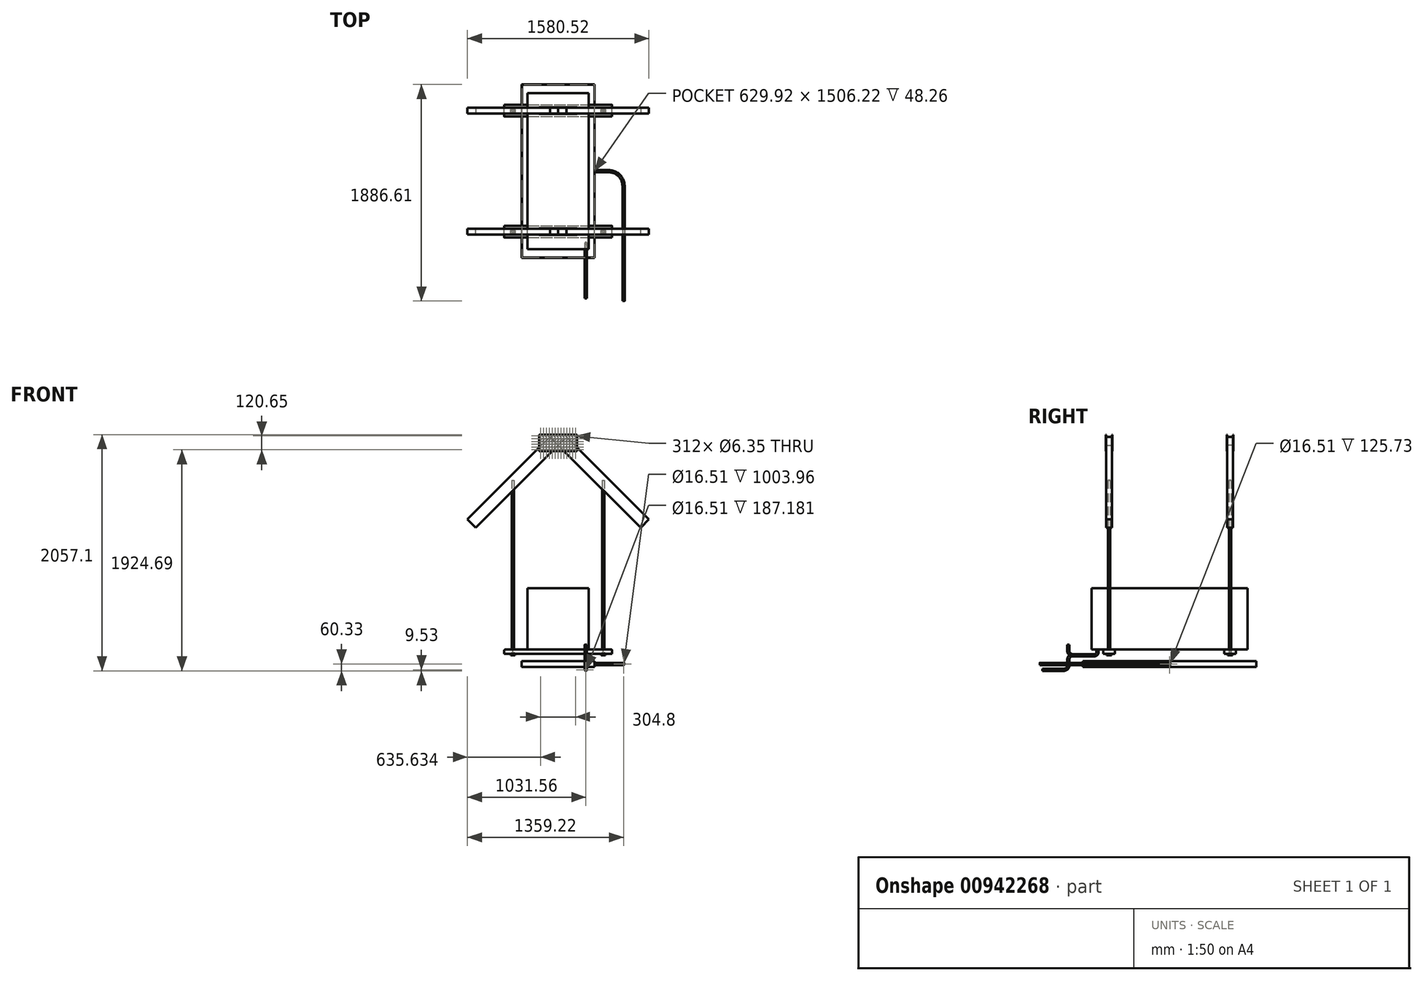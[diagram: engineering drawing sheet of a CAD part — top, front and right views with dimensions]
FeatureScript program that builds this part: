
annotation { "Feature Type Name" : "Feature", "Feature Type Description" : "" }
export const myFeature = defineFeature(function(context is Context, id is Id, definition is map)
    precondition{}
    {
        {
            var Q0;
            Q0=qCreatedBy(makeId("Front.planeOp"),FACE);
            var sketch = newSketch(context, id + "F0", { "sketchPlane" : qUnion([Q0])});
            skLineSegment(sketch, "E0.bottom", {"start": v(-266.7, 266.7) * mm, "end": v(266.7, 266.7) * mm});
            skLineSegment(sketch, "E0.top", {"start": v(-266.7, -266.7) * mm, "end": v(266.7, -266.7) * mm});
            skLineSegment(sketch, "E0.left", {"start": v(-266.7, 266.7) * mm, "end": v(-266.7, -266.7) * mm});
            skLineSegment(sketch, "E0.right", {"start": v(266.7, 266.7) * mm, "end": v(266.7, -266.7) * mm});
            skSolve(sketch);
        }
        {
            var Q0;
            Q0 = qSketchRegion(id + "F0", true);
            extrude(context, id + "F1", {"entities" : qUnion([Q0]), "endBound" : BoundingType.SYMMETRIC, "depth" : 1358.9 * mm, "offsetDistance" : 25.4 * mm});
        }
        {
            var Q0;
            Q0=makeQuery(id+"F1.opExtrude","SWEPT_FACE",FACE,{"disambiguationData":[OSD([sQuery(id+"F0.wireOp",EDGE,"E0.top")])]});
            var sketch = newSketch(context, id + "F2", { "sketchPlane" : qUnion([Q0])});
            skLineSegment(sketch, "E1.bottom", {"start": v(-469.9, 577.85) * mm, "end": v(469.9, 577.85) * mm});
            skLineSegment(sketch, "E1.top", {"start": v(-469.9, 476.25) * mm, "end": v(469.9, 476.25) * mm});
            skLineSegment(sketch, "E1.left", {"start": v(-469.9, 577.85) * mm, "end": v(-469.9, 476.25) * mm});
            skLineSegment(sketch, "E1.right", {"start": v(469.9, 577.85) * mm, "end": v(469.9, 476.25) * mm});
            skLineSegment(sketch, "E2.bottom", {"start": v(-469.9, -476.25) * mm, "end": v(469.9, -476.25) * mm});
            skLineSegment(sketch, "E2.top", {"start": v(-469.9, -577.85) * mm, "end": v(469.9, -577.85) * mm});
            skLineSegment(sketch, "E2.left", {"start": v(-469.9, -476.25) * mm, "end": v(-469.9, -577.85) * mm});
            skLineSegment(sketch, "E2.right", {"start": v(469.9, -476.25) * mm, "end": v(469.9, -577.85) * mm});
            skSolve(sketch);
        }
        {
            var Q0;
            Q0 = qSketchRegion(id + "F2", true);
            extrude(context, id + "F3", {"entities" : qUnion([Q0]), "operationType" : NewBodyOperationType.ADD, "depth" : 38.1 * mm, "offsetDistance" : 25.4 * mm});
        }
        {
            var Q0;
            {var subQ0=sQuery(id+"F2.wireOp",EDGE,"E1.top");var subQ1=sQuery(id+"F2.wireOp",EDGE,"E1.bottom");var subQ2=sQuery(id+"F2.wireOp",EDGE,"E1.right");Q0=makeQuery(id+"F3.boolean.opBoolean","SPLIT",FACE,{"disambiguationData":[TD([makeQuery(id+"F1.opExtrude","SWEPT_FACE",FACE,{"disambiguationData":[OSD([sQuery(id+"F0.wireOp",EDGE,"E0.right")])]})])],"derivedFrom":makeQuery(id+"F3.opExtrude","CAP_FACE",FACE,{"disambiguationData":[OSD([subQ1,subQ0,sQuery(id+"F2.wireOp",EDGE,"E1.left"),subQ2])],"isStart":true})});}
            var sketch = newSketch(context, id + "F4", { "sketchPlane" : qUnion([Q0])});
            skPoint(sketch, "E3", {"position": v(393.7, -527.05) * mm});
            skPoint(sketch, "E4", {"position": v(-393.7, -527.05) * mm});
            skSolve(sketch);
        }
        {
            var Q0;
            {var subQ0=sQuery(id+"F2.wireOp",EDGE,"E2.top");var subQ1=sQuery(id+"F2.wireOp",EDGE,"E2.bottom");var subQ2=sQuery(id+"F2.wireOp",EDGE,"E2.right");Q0=makeQuery(id+"F3.boolean.opBoolean","SPLIT",FACE,{"disambiguationData":[TD([makeQuery(id+"F1.opExtrude","SWEPT_FACE",FACE,{"disambiguationData":[OSD([sQuery(id+"F0.wireOp",EDGE,"E0.right")])]})])],"derivedFrom":makeQuery(id+"F3.opExtrude","CAP_FACE",FACE,{"disambiguationData":[OSD([subQ1,subQ0,sQuery(id+"F2.wireOp",EDGE,"E2.left"),subQ2])],"isStart":true})});}
            var sketch = newSketch(context, id + "F5", { "sketchPlane" : qUnion([Q0])});
            skPoint(sketch, "E5", {"position": v(393.7, 527.05) * mm});
            skPoint(sketch, "E6", {"position": v(-393.7, 527.05) * mm});
            skSolve(sketch);
        }
        {
            var Q0;
            Q0=sQuery(id+"F4.wireOp",VERTEX,"E3");
            var Q1;
            Q1=sQuery(id+"F4.wireOp",VERTEX,"E4");
            var Q2;
            Q2=sQuery(id+"F5.wireOp",VERTEX,"E5");
            var Q3;
            Q3=sQuery(id+"F5.wireOp",VERTEX,"E6");
            var Q4;
            Q4=makeQuery(id+"F1.opExtrude","SWEPT_BODY",BODY,{"disambiguationData":[OSD([sQuery(id+"F0.wireOp",EDGE,"E0.bottom"),sQuery(id+"F0.wireOp",EDGE,"E0.top"),sQuery(id+"F0.wireOp",EDGE,"E0.left"),sQuery(id+"F0.wireOp",EDGE,"E0.right")])]});
            hole(context, id + "F6", {"style" : HoleStyle.SIMPLE, "endStyle" : HoleEndStyle.THROUGH, "standardTappedOrClearance" : lookupTablePath({ "standard" : "ANSI", "size" : "3/4 (0.75)", "type" : "Drilled" }), "standardBlindInLast" : lookupTablePath({ "standard" : "ANSI", "size" : "3/4 (0.75)", "type" : "Drilled" }), "holeDiameter" : 3 / 101.6 * mm, "majorDiameter" : 6.35 * mm, "isTappedThrough" : true, "tappedDepth" : 12.7 * mm, "tapClearance" : 3, "locations" : qUnion([Q0, Q1, Q2, Q3]), "scope" : qUnion([Q4])});
        }
        {
            var Q0;
            Q0=makeQuery(id+"F3.opExtrude","CAP_EDGE",EDGE,{"disambiguationData":[OSD([sQuery(id+"F2.wireOp",EDGE,"E1.right")])],"isStart":true});
            var Q1;
            Q1=makeQuery(id+"F3.opExtrude","CAP_EDGE",EDGE,{"disambiguationData":[OSD([sQuery(id+"F2.wireOp",EDGE,"E2.right")])],"isStart":true});
            var Q2;
            Q2=makeQuery(id+"F3.opExtrude","CAP_EDGE",EDGE,{"disambiguationData":[OSD([sQuery(id+"F2.wireOp",EDGE,"E1.left")])],"isStart":true});
            var Q3;
            Q3=makeQuery(id+"F3.opExtrude","CAP_EDGE",EDGE,{"disambiguationData":[OSD([sQuery(id+"F2.wireOp",EDGE,"E2.left")])],"isStart":true});
            fillet(context, id + "F7", {"entities" : qUnion([Q0, Q1, Q2, Q3]), "radius" : 12.7 * mm, "tangentPropagation" : true, "allowEdgeOverflow" : false});
        }
        {
            var Q0;
            Q0=makeQuery(id+"F3.opExtrude","CAP_FACE",FACE,{"disambiguationData":[OSD([sQuery(id+"F2.wireOp",EDGE,"E1.bottom"),sQuery(id+"F2.wireOp",EDGE,"E1.top"),sQuery(id+"F2.wireOp",EDGE,"E1.left"),sQuery(id+"F2.wireOp",EDGE,"E1.right")])],"isStart":false});
            cPlane(context, id + "F8", {"entities" : qUnion([Q0]), "cplaneType" : CPlaneType.OFFSET, "offset" : 12.7 * mm, "width" : 152.4 * mm, "height" : 152.4 * mm});
        }
        {
            var Q0;
            Q0=qCreatedBy(id+"F8.planeOp",FACE);
            var sketch = newSketch(context, id + "F9", { "sketchPlane" : qUnion([Q0])});
            skCircle(sketch, "E7.0", {"center": v(393.7, 527.05) * mm, "radius": 9.53 * mm});
            skCircle(sketch, "E8.0", {"center": v(-393.7, 527.05) * mm, "radius": 9.53 * mm});
            skSolve(sketch);
        }
        {
            var Q0;
            Q0 = qSketchRegion(id + "F9", true);
            extrude(context, id + "F10", {"entities" : qUnion([Q0]), "operationType" : NewBodyOperationType.ADD, "oppositeDirection" : true, "depth" : 1524 * mm, "offsetDistance" : 25.4 * mm});
        }
        {
            var Q0;
            Q0=makeQuery(id+"F3.opExtrude","CAP_FACE",FACE,{"disambiguationData":[OSD([sQuery(id+"F2.wireOp",EDGE,"E2.bottom"),sQuery(id+"F2.wireOp",EDGE,"E2.top"),sQuery(id+"F2.wireOp",EDGE,"E2.left"),sQuery(id+"F2.wireOp",EDGE,"E2.right")])],"isStart":false});
            cPlane(context, id + "F11", {"entities" : qUnion([Q0]), "cplaneType" : CPlaneType.OFFSET, "offset" : 12.7 * mm, "width" : 152.4 * mm, "height" : 152.4 * mm});
        }
        {
            var Q0;
            Q0=qCreatedBy(id+"F11.planeOp",FACE);
            var sketch = newSketch(context, id + "F12", { "sketchPlane" : qUnion([Q0])});
            skCircle(sketch, "E9.0", {"center": v(-393.7, -527.05) * mm, "radius": 9.53 * mm});
            skCircle(sketch, "E10.0", {"center": v(393.7, -527.05) * mm, "radius": 9.53 * mm});
            skSolve(sketch);
        }
        {
            var Q0;
            Q0 = qSketchRegion(id + "F12", true);
            extrude(context, id + "F13", {"entities" : qUnion([Q0]), "oppositeDirection" : true, "depth" : 1524 * mm, "offsetDistance" : 25.4 * mm});
        }
        {
            var Q0;
            Q0=makeQuery(id+"F1.opExtrude","CAP_FACE",FACE,{"disambiguationData":[OSD([sQuery(id+"F0.wireOp",EDGE,"E0.bottom"),sQuery(id+"F0.wireOp",EDGE,"E0.top"),sQuery(id+"F0.wireOp",EDGE,"E0.left"),sQuery(id+"F0.wireOp",EDGE,"E0.right")])],"isStart":false});
            cPlane(context, id + "F14", {"entities" : qUnion([Q0]), "cplaneType" : CPlaneType.OFFSET, "offset" : 152.4 * mm, "oppositeDirection" : true, "width" : 152.4 * mm, "height" : 152.4 * mm});
        }
        {
            var Q0;
            Q0=qCreatedBy(id+"F14.planeOp",FACE);
            var sketch = newSketch(context, id + "F15", { "sketchPlane" : qUnion([Q0])});
            skLineSegment(sketch, "E11", {"start": v(0, 2010.8) * mm, "end": v(0, -441.63) * mm, "construction": true});
            skLineSegment(sketch, "E12", {"start": v(0, 1511.3) * mm, "end": v(718.42, 792.88) * mm});
            skLineSegment(sketch, "E13", {"start": v(718.42, 792.88) * mm, "end": v(790.26, 864.72) * mm});
            skLineSegment(sketch, "E14", {"start": v(0, 1511.3) * mm, "end": v(71.84, 1583.14) * mm});
            skLineSegment(sketch, "E15", {"start": v(790.26, 864.72) * mm, "end": v(71.84, 1583.14) * mm});
            skLineSegment(sketch, "E16", {"start": v(0, 1511.3) * mm, "end": v(-718.42, 792.88) * mm});
            skLineSegment(sketch, "E17", {"start": v(-718.42, 792.88) * mm, "end": v(-790.26, 864.72) * mm});
            skLineSegment(sketch, "E18", {"start": v(0, 1511.3) * mm, "end": v(-71.84, 1583.14) * mm});
            skLineSegment(sketch, "E19", {"start": v(-790.26, 864.72) * mm, "end": v(-71.84, 1583.14) * mm});
            skSolve(sketch);
        }
        {
            var Q0;
            Q0 = qSketchRegion(id + "F15", true);
            extrude(context, id + "F16", {"entities" : qUnion([Q0]), "endBound" : BoundingType.SYMMETRIC, "depth" : 50.8 * mm, "offsetDistance" : 25.4 * mm});
        }
        {
            var Q0;
            Q0=makeQuery(id+"F1.opExtrude","CAP_FACE",FACE,{"disambiguationData":[OSD([sQuery(id+"F0.wireOp",EDGE,"E0.bottom"),sQuery(id+"F0.wireOp",EDGE,"E0.top"),sQuery(id+"F0.wireOp",EDGE,"E0.left"),sQuery(id+"F0.wireOp",EDGE,"E0.right")])],"isStart":false});
            cPlane(context, id + "F17", {"entities" : qUnion([Q0]), "cplaneType" : CPlaneType.OFFSET, "offset" : 679.45 * mm, "oppositeDirection" : true, "width" : 152.4 * mm, "height" : 152.4 * mm});
        }
        {
            var Q0;
            Q0=makeQuery(id+"F16.opExtrude","SWEPT_BODY",BODY,{"disambiguationData":[OSD([sQuery(id+"F15.wireOp",EDGE,"E12"),sQuery(id+"F15.wireOp",EDGE,"E13"),sQuery(id+"F15.wireOp",EDGE,"E14"),sQuery(id+"F15.wireOp",EDGE,"E15")])]});
            var Q1;
            Q1=makeQuery(id+"F16.opExtrude","SWEPT_BODY",BODY,{"disambiguationData":[OSD([sQuery(id+"F15.wireOp",EDGE,"E16"),sQuery(id+"F15.wireOp",EDGE,"E17"),sQuery(id+"F15.wireOp",EDGE,"E18"),sQuery(id+"F15.wireOp",EDGE,"E19")])]});
            var Q2;
            Q2=qCreatedBy(id+"F17.planeOp",FACE);
            mirror(context, id + "F18", {"entities" : qUnion([Q0, Q1]), "mirrorPlane" : qUnion([Q2])});
        }
        {
            var Q0;
            Q0=makeQuery(id+"F16.opExtrude","CAP_FACE",FACE,{"disambiguationData":[OSD([sQuery(id+"F15.wireOp",EDGE,"E12"),sQuery(id+"F15.wireOp",EDGE,"E13"),sQuery(id+"F15.wireOp",EDGE,"E14"),sQuery(id+"F15.wireOp",EDGE,"E15")])],"isStart":false});
            var sketch = newSketch(context, id + "F19", { "sketchPlane" : qUnion([Q0])});
            skLineSegment(sketch, "E20.bottom", {"start": v(-165.1, 1603.07) * mm, "end": v(165.1, 1603.07) * mm});
            skLineSegment(sketch, "E20.top", {"start": v(-165.1, 1460.5) * mm, "end": v(165.1, 1460.5) * mm});
            skLineSegment(sketch, "E20.left", {"start": v(-165.1, 1603.07) * mm, "end": v(-165.1, 1460.5) * mm});
            skLineSegment(sketch, "E20.right", {"start": v(165.1, 1603.07) * mm, "end": v(165.1, 1460.5) * mm});
            skCircle(sketch, "E21", {"center": v(-154.63, 1470.66) * mm, "radius": 3.18 * mm});
            skCircle(sketch, "E22.0.1.0", {"center": v(-154.63, 1494.8) * mm, "radius": 3.18 * mm});
            skCircle(sketch, "E22.0.2.0", {"center": v(-154.63, 1518.92) * mm, "radius": 3.18 * mm});
            skCircle(sketch, "E22.0.3.0", {"center": v(-154.63, 1543.05) * mm, "radius": 3.18 * mm});
            skCircle(sketch, "E22.0.4.0", {"center": v(-154.63, 1567.18) * mm, "radius": 3.18 * mm});
            skCircle(sketch, "E22.0.5.0", {"center": v(-154.63, 1591.3) * mm, "radius": 3.18 * mm});
            skCircle(sketch, "E22.1.0.0", {"center": v(-129.23, 1470.66) * mm, "radius": 3.18 * mm});
            skCircle(sketch, "E22.1.1.0", {"center": v(-129.23, 1494.8) * mm, "radius": 3.18 * mm});
            skCircle(sketch, "E22.1.2.0", {"center": v(-129.23, 1518.92) * mm, "radius": 3.18 * mm});
            skCircle(sketch, "E22.1.3.0", {"center": v(-129.23, 1543.05) * mm, "radius": 3.18 * mm});
            skCircle(sketch, "E22.1.4.0", {"center": v(-129.23, 1567.18) * mm, "radius": 3.18 * mm});
            skCircle(sketch, "E22.1.5.0", {"center": v(-129.23, 1591.3) * mm, "radius": 3.18 * mm});
            skCircle(sketch, "E22.2.0.0", {"center": v(-103.83, 1470.66) * mm, "radius": 3.18 * mm});
            skCircle(sketch, "E22.2.1.0", {"center": v(-103.83, 1494.8) * mm, "radius": 3.18 * mm});
            skCircle(sketch, "E22.2.2.0", {"center": v(-103.83, 1518.92) * mm, "radius": 3.18 * mm});
            skCircle(sketch, "E22.2.3.0", {"center": v(-103.83, 1543.05) * mm, "radius": 3.18 * mm});
            skCircle(sketch, "E22.2.4.0", {"center": v(-103.83, 1567.18) * mm, "radius": 3.18 * mm});
            skCircle(sketch, "E22.2.5.0", {"center": v(-103.83, 1591.3) * mm, "radius": 3.18 * mm});
            skCircle(sketch, "E22.3.0.0", {"center": v(-78.43, 1470.66) * mm, "radius": 3.18 * mm});
            skCircle(sketch, "E22.3.1.0", {"center": v(-78.43, 1494.8) * mm, "radius": 3.18 * mm});
            skCircle(sketch, "E22.3.2.0", {"center": v(-78.43, 1518.92) * mm, "radius": 3.18 * mm});
            skCircle(sketch, "E22.3.3.0", {"center": v(-78.43, 1543.05) * mm, "radius": 3.18 * mm});
            skCircle(sketch, "E22.3.4.0", {"center": v(-78.43, 1567.18) * mm, "radius": 3.18 * mm});
            skCircle(sketch, "E22.3.5.0", {"center": v(-78.43, 1591.3) * mm, "radius": 3.18 * mm});
            skCircle(sketch, "E22.4.0.0", {"center": v(-53.03, 1470.66) * mm, "radius": 3.18 * mm});
            skCircle(sketch, "E22.4.1.0", {"center": v(-53.03, 1494.8) * mm, "radius": 3.18 * mm});
            skCircle(sketch, "E22.4.2.0", {"center": v(-53.03, 1518.92) * mm, "radius": 3.18 * mm});
            skCircle(sketch, "E22.4.3.0", {"center": v(-53.03, 1543.05) * mm, "radius": 3.18 * mm});
            skCircle(sketch, "E22.4.4.0", {"center": v(-53.03, 1567.18) * mm, "radius": 3.18 * mm});
            skCircle(sketch, "E22.4.5.0", {"center": v(-53.03, 1591.3) * mm, "radius": 3.18 * mm});
            skCircle(sketch, "E22.5.0.0", {"center": v(-27.63, 1470.66) * mm, "radius": 3.18 * mm});
            skCircle(sketch, "E22.5.1.0", {"center": v(-27.63, 1494.8) * mm, "radius": 3.18 * mm});
            skCircle(sketch, "E22.5.2.0", {"center": v(-27.63, 1518.92) * mm, "radius": 3.18 * mm});
            skCircle(sketch, "E22.5.3.0", {"center": v(-27.63, 1543.05) * mm, "radius": 3.18 * mm});
            skCircle(sketch, "E22.5.4.0", {"center": v(-27.63, 1567.18) * mm, "radius": 3.18 * mm});
            skCircle(sketch, "E22.5.5.0", {"center": v(-27.63, 1591.3) * mm, "radius": 3.18 * mm});
            skCircle(sketch, "E22.6.0.0", {"center": v(-2.23, 1470.66) * mm, "radius": 3.18 * mm});
            skCircle(sketch, "E22.6.1.0", {"center": v(-2.23, 1494.8) * mm, "radius": 3.18 * mm});
            skCircle(sketch, "E22.6.2.0", {"center": v(-2.23, 1518.92) * mm, "radius": 3.18 * mm});
            skCircle(sketch, "E22.6.3.0", {"center": v(-2.23, 1543.05) * mm, "radius": 3.18 * mm});
            skCircle(sketch, "E22.6.4.0", {"center": v(-2.23, 1567.18) * mm, "radius": 3.18 * mm});
            skCircle(sketch, "E22.6.5.0", {"center": v(-2.23, 1591.3) * mm, "radius": 3.18 * mm});
            skCircle(sketch, "E22.7.0.0", {"center": v(23.17, 1470.66) * mm, "radius": 3.18 * mm});
            skCircle(sketch, "E22.7.1.0", {"center": v(23.17, 1494.8) * mm, "radius": 3.18 * mm});
            skCircle(sketch, "E22.7.2.0", {"center": v(23.17, 1518.92) * mm, "radius": 3.18 * mm});
            skCircle(sketch, "E22.7.3.0", {"center": v(23.17, 1543.05) * mm, "radius": 3.18 * mm});
            skCircle(sketch, "E22.7.4.0", {"center": v(23.17, 1567.18) * mm, "radius": 3.18 * mm});
            skCircle(sketch, "E22.7.5.0", {"center": v(23.17, 1591.3) * mm, "radius": 3.18 * mm});
            skCircle(sketch, "E22.8.0.0", {"center": v(48.57, 1470.66) * mm, "radius": 3.18 * mm});
            skCircle(sketch, "E22.8.1.0", {"center": v(48.57, 1494.8) * mm, "radius": 3.18 * mm});
            skCircle(sketch, "E22.8.2.0", {"center": v(48.57, 1518.92) * mm, "radius": 3.18 * mm});
            skCircle(sketch, "E22.8.3.0", {"center": v(48.57, 1543.05) * mm, "radius": 3.18 * mm});
            skCircle(sketch, "E22.8.4.0", {"center": v(48.57, 1567.18) * mm, "radius": 3.18 * mm});
            skCircle(sketch, "E22.8.5.0", {"center": v(48.57, 1591.3) * mm, "radius": 3.18 * mm});
            skCircle(sketch, "E22.9.0.0", {"center": v(73.97, 1470.66) * mm, "radius": 3.18 * mm});
            skCircle(sketch, "E22.9.1.0", {"center": v(73.97, 1494.8) * mm, "radius": 3.18 * mm});
            skCircle(sketch, "E22.9.2.0", {"center": v(73.97, 1518.92) * mm, "radius": 3.18 * mm});
            skCircle(sketch, "E22.9.3.0", {"center": v(73.97, 1543.05) * mm, "radius": 3.18 * mm});
            skCircle(sketch, "E22.9.4.0", {"center": v(73.97, 1567.18) * mm, "radius": 3.18 * mm});
            skCircle(sketch, "E22.9.5.0", {"center": v(73.97, 1591.3) * mm, "radius": 3.18 * mm});
            skCircle(sketch, "E22.10.0.0", {"center": v(99.37, 1470.66) * mm, "radius": 3.18 * mm});
            skCircle(sketch, "E22.10.1.0", {"center": v(99.37, 1494.8) * mm, "radius": 3.18 * mm});
            skCircle(sketch, "E22.10.2.0", {"center": v(99.37, 1518.92) * mm, "radius": 3.18 * mm});
            skCircle(sketch, "E22.10.3.0", {"center": v(99.37, 1543.05) * mm, "radius": 3.18 * mm});
            skCircle(sketch, "E22.10.4.0", {"center": v(99.37, 1567.18) * mm, "radius": 3.18 * mm});
            skCircle(sketch, "E22.10.5.0", {"center": v(99.37, 1591.3) * mm, "radius": 3.18 * mm});
            skCircle(sketch, "E22.11.0.0", {"center": v(124.77, 1470.66) * mm, "radius": 3.18 * mm});
            skCircle(sketch, "E22.11.1.0", {"center": v(124.77, 1494.8) * mm, "radius": 3.18 * mm});
            skCircle(sketch, "E22.11.2.0", {"center": v(124.77, 1518.92) * mm, "radius": 3.18 * mm});
            skCircle(sketch, "E22.11.3.0", {"center": v(124.77, 1543.05) * mm, "radius": 3.18 * mm});
            skCircle(sketch, "E22.11.4.0", {"center": v(124.77, 1567.18) * mm, "radius": 3.18 * mm});
            skCircle(sketch, "E22.11.5.0", {"center": v(124.77, 1591.3) * mm, "radius": 3.18 * mm});
            skCircle(sketch, "E22.12.0.0", {"center": v(150.17, 1470.66) * mm, "radius": 3.18 * mm});
            skCircle(sketch, "E22.12.1.0", {"center": v(150.17, 1494.8) * mm, "radius": 3.18 * mm});
            skCircle(sketch, "E22.12.2.0", {"center": v(150.17, 1518.92) * mm, "radius": 3.18 * mm});
            skCircle(sketch, "E22.12.3.0", {"center": v(150.17, 1543.05) * mm, "radius": 3.18 * mm});
            skCircle(sketch, "E22.12.4.0", {"center": v(150.17, 1567.18) * mm, "radius": 3.18 * mm});
            skCircle(sketch, "E22.12.5.0", {"center": v(150.17, 1591.3) * mm, "radius": 3.18 * mm});
            skLineSegment(sketch, "E22.direction1", {"start": v(-154.63, 1470.66) * mm, "end": v(-129.23, 1470.66) * mm, "construction": true});
            skLineSegment(sketch, "E22.direction2", {"start": v(-154.63, 1470.66) * mm, "end": v(-154.63, 1494.8) * mm, "construction": true});
            skSolve(sketch);
        }
        {
            var Q0;
            Q0 = qSketchRegion(id + "F19", true);
            extrude(context, id + "F20", {"entities" : qUnion([Q0]), "depth" : 2.54 * mm, "offsetDistance" : 25.4 * mm});
        }
        {
            var Q0;
            Q0=makeQuery(id+"F16.opExtrude","CAP_FACE",FACE,{"disambiguationData":[OSD([sQuery(id+"F15.wireOp",EDGE,"E12"),sQuery(id+"F15.wireOp",EDGE,"E13"),sQuery(id+"F15.wireOp",EDGE,"E14"),sQuery(id+"F15.wireOp",EDGE,"E15")])],"isStart":true});
            var sketch = newSketch(context, id + "F21", { "sketchPlane" : qUnion([Q0])});
            skLineSegment(sketch, "E23.0.0", {"start": v(165.1, 1460.5) * mm, "end": v(165.1, 1603.07) * mm});
            skLineSegment(sketch, "E23.0.1", {"start": v(165.1, 1603.07) * mm, "end": v(-165.1, 1603.07) * mm});
            skLineSegment(sketch, "E23.0.2", {"start": v(-165.1, 1603.07) * mm, "end": v(-165.1, 1460.5) * mm});
            skLineSegment(sketch, "E23.0.3", {"start": v(-165.1, 1460.5) * mm, "end": v(165.1, 1460.5) * mm});
            skCircle(sketch, "E24.0", {"center": v(154.63, 1591.3) * mm, "radius": 3.18 * mm});
            skCircle(sketch, "E25.0.1.0", {"center": v(154.63, 1567.18) * mm, "radius": 3.18 * mm});
            skCircle(sketch, "E25.0.2.0", {"center": v(154.63, 1543.05) * mm, "radius": 3.18 * mm});
            skCircle(sketch, "E25.0.3.0", {"center": v(154.63, 1518.92) * mm, "radius": 3.18 * mm});
            skCircle(sketch, "E25.0.4.0", {"center": v(154.63, 1494.8) * mm, "radius": 3.18 * mm});
            skCircle(sketch, "E25.0.5.0", {"center": v(154.63, 1470.66) * mm, "radius": 3.18 * mm});
            skCircle(sketch, "E25.1.0.0", {"center": v(129.23, 1591.3) * mm, "radius": 3.18 * mm});
            skCircle(sketch, "E25.1.1.0", {"center": v(129.23, 1567.18) * mm, "radius": 3.18 * mm});
            skCircle(sketch, "E25.1.2.0", {"center": v(129.23, 1543.05) * mm, "radius": 3.18 * mm});
            skCircle(sketch, "E25.1.3.0", {"center": v(129.23, 1518.92) * mm, "radius": 3.18 * mm});
            skCircle(sketch, "E25.1.4.0", {"center": v(129.23, 1494.8) * mm, "radius": 3.18 * mm});
            skCircle(sketch, "E25.1.5.0", {"center": v(129.23, 1470.66) * mm, "radius": 3.18 * mm});
            skCircle(sketch, "E25.2.0.0", {"center": v(103.83, 1591.3) * mm, "radius": 3.18 * mm});
            skCircle(sketch, "E25.2.1.0", {"center": v(103.83, 1567.18) * mm, "radius": 3.18 * mm});
            skCircle(sketch, "E25.2.2.0", {"center": v(103.83, 1543.05) * mm, "radius": 3.18 * mm});
            skCircle(sketch, "E25.2.3.0", {"center": v(103.83, 1518.92) * mm, "radius": 3.18 * mm});
            skCircle(sketch, "E25.2.4.0", {"center": v(103.83, 1494.8) * mm, "radius": 3.18 * mm});
            skCircle(sketch, "E25.2.5.0", {"center": v(103.83, 1470.66) * mm, "radius": 3.18 * mm});
            skCircle(sketch, "E25.3.0.0", {"center": v(78.43, 1591.3) * mm, "radius": 3.18 * mm});
            skCircle(sketch, "E25.3.1.0", {"center": v(78.43, 1567.18) * mm, "radius": 3.18 * mm});
            skCircle(sketch, "E25.3.2.0", {"center": v(78.43, 1543.05) * mm, "radius": 3.18 * mm});
            skCircle(sketch, "E25.3.3.0", {"center": v(78.43, 1518.92) * mm, "radius": 3.18 * mm});
            skCircle(sketch, "E25.3.4.0", {"center": v(78.43, 1494.8) * mm, "radius": 3.18 * mm});
            skCircle(sketch, "E25.3.5.0", {"center": v(78.43, 1470.66) * mm, "radius": 3.18 * mm});
            skCircle(sketch, "E25.4.0.0", {"center": v(53.03, 1591.3) * mm, "radius": 3.18 * mm});
            skCircle(sketch, "E25.4.1.0", {"center": v(53.03, 1567.18) * mm, "radius": 3.18 * mm});
            skCircle(sketch, "E25.4.2.0", {"center": v(53.03, 1543.05) * mm, "radius": 3.18 * mm});
            skCircle(sketch, "E25.4.3.0", {"center": v(53.03, 1518.92) * mm, "radius": 3.18 * mm});
            skCircle(sketch, "E25.4.4.0", {"center": v(53.03, 1494.8) * mm, "radius": 3.18 * mm});
            skCircle(sketch, "E25.4.5.0", {"center": v(53.03, 1470.66) * mm, "radius": 3.18 * mm});
            skCircle(sketch, "E25.5.0.0", {"center": v(27.63, 1591.3) * mm, "radius": 3.18 * mm});
            skCircle(sketch, "E25.5.1.0", {"center": v(27.63, 1567.18) * mm, "radius": 3.18 * mm});
            skCircle(sketch, "E25.5.2.0", {"center": v(27.63, 1543.05) * mm, "radius": 3.18 * mm});
            skCircle(sketch, "E25.5.3.0", {"center": v(27.63, 1518.92) * mm, "radius": 3.18 * mm});
            skCircle(sketch, "E25.5.4.0", {"center": v(27.63, 1494.8) * mm, "radius": 3.18 * mm});
            skCircle(sketch, "E25.5.5.0", {"center": v(27.63, 1470.66) * mm, "radius": 3.18 * mm});
            skCircle(sketch, "E25.6.0.0", {"center": v(2.23, 1591.3) * mm, "radius": 3.18 * mm});
            skCircle(sketch, "E25.6.1.0", {"center": v(2.23, 1567.18) * mm, "radius": 3.18 * mm});
            skCircle(sketch, "E25.6.2.0", {"center": v(2.23, 1543.05) * mm, "radius": 3.18 * mm});
            skCircle(sketch, "E25.6.3.0", {"center": v(2.23, 1518.92) * mm, "radius": 3.18 * mm});
            skCircle(sketch, "E25.6.4.0", {"center": v(2.23, 1494.8) * mm, "radius": 3.18 * mm});
            skCircle(sketch, "E25.6.5.0", {"center": v(2.23, 1470.66) * mm, "radius": 3.18 * mm});
            skCircle(sketch, "E25.7.0.0", {"center": v(-23.17, 1591.3) * mm, "radius": 3.18 * mm});
            skCircle(sketch, "E25.7.1.0", {"center": v(-23.17, 1567.18) * mm, "radius": 3.18 * mm});
            skCircle(sketch, "E25.7.2.0", {"center": v(-23.17, 1543.05) * mm, "radius": 3.18 * mm});
            skCircle(sketch, "E25.7.3.0", {"center": v(-23.17, 1518.92) * mm, "radius": 3.18 * mm});
            skCircle(sketch, "E25.7.4.0", {"center": v(-23.17, 1494.8) * mm, "radius": 3.18 * mm});
            skCircle(sketch, "E25.7.5.0", {"center": v(-23.17, 1470.66) * mm, "radius": 3.18 * mm});
            skCircle(sketch, "E25.8.0.0", {"center": v(-48.57, 1591.3) * mm, "radius": 3.18 * mm});
            skCircle(sketch, "E25.8.1.0", {"center": v(-48.57, 1567.18) * mm, "radius": 3.18 * mm});
            skCircle(sketch, "E25.8.2.0", {"center": v(-48.57, 1543.05) * mm, "radius": 3.18 * mm});
            skCircle(sketch, "E25.8.3.0", {"center": v(-48.57, 1518.92) * mm, "radius": 3.18 * mm});
            skCircle(sketch, "E25.8.4.0", {"center": v(-48.57, 1494.8) * mm, "radius": 3.18 * mm});
            skCircle(sketch, "E25.8.5.0", {"center": v(-48.57, 1470.66) * mm, "radius": 3.18 * mm});
            skCircle(sketch, "E25.9.0.0", {"center": v(-73.97, 1591.3) * mm, "radius": 3.18 * mm});
            skCircle(sketch, "E25.9.1.0", {"center": v(-73.97, 1567.18) * mm, "radius": 3.18 * mm});
            skCircle(sketch, "E25.9.2.0", {"center": v(-73.97, 1543.05) * mm, "radius": 3.18 * mm});
            skCircle(sketch, "E25.9.3.0", {"center": v(-73.97, 1518.92) * mm, "radius": 3.18 * mm});
            skCircle(sketch, "E25.9.4.0", {"center": v(-73.97, 1494.8) * mm, "radius": 3.18 * mm});
            skCircle(sketch, "E25.9.5.0", {"center": v(-73.97, 1470.66) * mm, "radius": 3.18 * mm});
            skCircle(sketch, "E25.10.0.0", {"center": v(-99.37, 1591.3) * mm, "radius": 3.18 * mm});
            skCircle(sketch, "E25.10.1.0", {"center": v(-99.37, 1567.18) * mm, "radius": 3.18 * mm});
            skCircle(sketch, "E25.10.2.0", {"center": v(-99.37, 1543.05) * mm, "radius": 3.18 * mm});
            skCircle(sketch, "E25.10.3.0", {"center": v(-99.37, 1518.92) * mm, "radius": 3.18 * mm});
            skCircle(sketch, "E25.10.4.0", {"center": v(-99.37, 1494.8) * mm, "radius": 3.18 * mm});
            skCircle(sketch, "E25.10.5.0", {"center": v(-99.37, 1470.66) * mm, "radius": 3.18 * mm});
            skCircle(sketch, "E25.11.0.0", {"center": v(-124.77, 1591.3) * mm, "radius": 3.18 * mm});
            skCircle(sketch, "E25.11.1.0", {"center": v(-124.77, 1567.18) * mm, "radius": 3.18 * mm});
            skCircle(sketch, "E25.11.2.0", {"center": v(-124.77, 1543.05) * mm, "radius": 3.18 * mm});
            skCircle(sketch, "E25.11.3.0", {"center": v(-124.77, 1518.92) * mm, "radius": 3.18 * mm});
            skCircle(sketch, "E25.11.4.0", {"center": v(-124.77, 1494.8) * mm, "radius": 3.18 * mm});
            skCircle(sketch, "E25.11.5.0", {"center": v(-124.77, 1470.66) * mm, "radius": 3.18 * mm});
            skCircle(sketch, "E25.12.0.0", {"center": v(-150.17, 1591.3) * mm, "radius": 3.18 * mm});
            skCircle(sketch, "E25.12.1.0", {"center": v(-150.17, 1567.18) * mm, "radius": 3.18 * mm});
            skCircle(sketch, "E25.12.2.0", {"center": v(-150.17, 1543.05) * mm, "radius": 3.18 * mm});
            skCircle(sketch, "E25.12.3.0", {"center": v(-150.17, 1518.92) * mm, "radius": 3.18 * mm});
            skCircle(sketch, "E25.12.4.0", {"center": v(-150.17, 1494.8) * mm, "radius": 3.18 * mm});
            skCircle(sketch, "E25.12.5.0", {"center": v(-150.17, 1470.66) * mm, "radius": 3.18 * mm});
            skLineSegment(sketch, "E25.direction1", {"start": v(154.63, 1591.3) * mm, "end": v(129.23, 1591.3) * mm, "construction": true});
            skLineSegment(sketch, "E25.direction2", {"start": v(154.63, 1591.3) * mm, "end": v(154.63, 1567.18) * mm, "construction": true});
            skSolve(sketch);
        }
        {
            var Q0;
            Q0 = qSketchRegion(id + "F21", true);
            extrude(context, id + "F22", {"entities" : qUnion([Q0]), "depth" : 2.54 * mm, "offsetDistance" : 25.4 * mm});
        }
        {
            var Q0;
            Q0=makeQuery(id+"F20.opExtrude","SWEPT_BODY",BODY,{"disambiguationData":[OSD([sQuery(id+"F19.wireOp",EDGE,"E20.bottom"),sQuery(id+"F19.wireOp",EDGE,"E20.top"),sQuery(id+"F19.wireOp",EDGE,"E20.left"),sQuery(id+"F19.wireOp",EDGE,"E20.right"),sQuery(id+"F19.wireOp",EDGE,"E21"),sQuery(id+"F19.wireOp",EDGE,"E22.0.1.0"),sQuery(id+"F19.wireOp",EDGE,"E22.0.2.0"),sQuery(id+"F19.wireOp",EDGE,"E22.0.3.0"),sQuery(id+"F19.wireOp",EDGE,"E22.0.4.0"),sQuery(id+"F19.wireOp",EDGE,"E22.0.5.0"),sQuery(id+"F19.wireOp",EDGE,"E22.1.0.0"),sQuery(id+"F19.wireOp",EDGE,"E22.1.1.0"),sQuery(id+"F19.wireOp",EDGE,"E22.1.2.0"),sQuery(id+"F19.wireOp",EDGE,"E22.1.3.0"),sQuery(id+"F19.wireOp",EDGE,"E22.1.4.0"),sQuery(id+"F19.wireOp",EDGE,"E22.1.5.0"),sQuery(id+"F19.wireOp",EDGE,"E22.2.0.0"),sQuery(id+"F19.wireOp",EDGE,"E22.2.1.0"),sQuery(id+"F19.wireOp",EDGE,"E22.2.2.0"),sQuery(id+"F19.wireOp",EDGE,"E22.2.3.0"),sQuery(id+"F19.wireOp",EDGE,"E22.2.4.0"),sQuery(id+"F19.wireOp",EDGE,"E22.2.5.0"),sQuery(id+"F19.wireOp",EDGE,"E22.3.0.0"),sQuery(id+"F19.wireOp",EDGE,"E22.3.1.0"),sQuery(id+"F19.wireOp",EDGE,"E22.3.2.0"),sQuery(id+"F19.wireOp",EDGE,"E22.3.3.0"),sQuery(id+"F19.wireOp",EDGE,"E22.3.4.0"),sQuery(id+"F19.wireOp",EDGE,"E22.3.5.0"),sQuery(id+"F19.wireOp",EDGE,"E22.4.0.0"),sQuery(id+"F19.wireOp",EDGE,"E22.4.1.0"),sQuery(id+"F19.wireOp",EDGE,"E22.4.2.0"),sQuery(id+"F19.wireOp",EDGE,"E22.4.3.0"),sQuery(id+"F19.wireOp",EDGE,"E22.4.4.0"),sQuery(id+"F19.wireOp",EDGE,"E22.4.5.0"),sQuery(id+"F19.wireOp",EDGE,"E22.5.0.0"),sQuery(id+"F19.wireOp",EDGE,"E22.5.1.0"),sQuery(id+"F19.wireOp",EDGE,"E22.5.2.0"),sQuery(id+"F19.wireOp",EDGE,"E22.5.3.0"),sQuery(id+"F19.wireOp",EDGE,"E22.5.4.0"),sQuery(id+"F19.wireOp",EDGE,"E22.5.5.0"),sQuery(id+"F19.wireOp",EDGE,"E22.6.0.0"),sQuery(id+"F19.wireOp",EDGE,"E22.6.1.0"),sQuery(id+"F19.wireOp",EDGE,"E22.6.2.0"),sQuery(id+"F19.wireOp",EDGE,"E22.6.3.0"),sQuery(id+"F19.wireOp",EDGE,"E22.6.4.0"),sQuery(id+"F19.wireOp",EDGE,"E22.6.5.0"),sQuery(id+"F19.wireOp",EDGE,"E22.7.0.0"),sQuery(id+"F19.wireOp",EDGE,"E22.7.1.0"),sQuery(id+"F19.wireOp",EDGE,"E22.7.2.0"),sQuery(id+"F19.wireOp",EDGE,"E22.7.3.0"),sQuery(id+"F19.wireOp",EDGE,"E22.7.4.0"),sQuery(id+"F19.wireOp",EDGE,"E22.7.5.0"),sQuery(id+"F19.wireOp",EDGE,"E22.8.0.0"),sQuery(id+"F19.wireOp",EDGE,"E22.8.1.0"),sQuery(id+"F19.wireOp",EDGE,"E22.8.2.0"),sQuery(id+"F19.wireOp",EDGE,"E22.8.3.0"),sQuery(id+"F19.wireOp",EDGE,"E22.8.4.0"),sQuery(id+"F19.wireOp",EDGE,"E22.8.5.0"),sQuery(id+"F19.wireOp",EDGE,"E22.9.0.0"),sQuery(id+"F19.wireOp",EDGE,"E22.9.1.0"),sQuery(id+"F19.wireOp",EDGE,"E22.9.2.0"),sQuery(id+"F19.wireOp",EDGE,"E22.9.3.0"),sQuery(id+"F19.wireOp",EDGE,"E22.9.4.0"),sQuery(id+"F19.wireOp",EDGE,"E22.9.5.0"),sQuery(id+"F19.wireOp",EDGE,"E22.10.0.0"),sQuery(id+"F19.wireOp",EDGE,"E22.10.1.0"),sQuery(id+"F19.wireOp",EDGE,"E22.10.2.0"),sQuery(id+"F19.wireOp",EDGE,"E22.10.3.0"),sQuery(id+"F19.wireOp",EDGE,"E22.10.4.0"),sQuery(id+"F19.wireOp",EDGE,"E22.10.5.0"),sQuery(id+"F19.wireOp",EDGE,"E22.11.0.0"),sQuery(id+"F19.wireOp",EDGE,"E22.11.1.0"),sQuery(id+"F19.wireOp",EDGE,"E22.11.2.0"),sQuery(id+"F19.wireOp",EDGE,"E22.11.3.0"),sQuery(id+"F19.wireOp",EDGE,"E22.11.4.0"),sQuery(id+"F19.wireOp",EDGE,"E22.11.5.0"),sQuery(id+"F19.wireOp",EDGE,"E22.12.0.0"),sQuery(id+"F19.wireOp",EDGE,"E22.12.1.0"),sQuery(id+"F19.wireOp",EDGE,"E22.12.2.0"),sQuery(id+"F19.wireOp",EDGE,"E22.12.3.0"),sQuery(id+"F19.wireOp",EDGE,"E22.12.4.0"),sQuery(id+"F19.wireOp",EDGE,"E22.12.5.0")])]});
            var Q1;
            Q1=makeQuery(id+"F22.opExtrude","SWEPT_BODY",BODY,{"disambiguationData":[OSD([sQuery(id+"F21.wireOp",EDGE,"E23.0.0"),sQuery(id+"F21.wireOp",EDGE,"E23.0.1"),sQuery(id+"F21.wireOp",EDGE,"E23.0.2"),sQuery(id+"F21.wireOp",EDGE,"E23.0.3"),sQuery(id+"F21.wireOp",EDGE,"E24.0"),sQuery(id+"F21.wireOp",EDGE,"E25.0.1.0"),sQuery(id+"F21.wireOp",EDGE,"E25.0.2.0"),sQuery(id+"F21.wireOp",EDGE,"E25.0.3.0"),sQuery(id+"F21.wireOp",EDGE,"E25.0.4.0"),sQuery(id+"F21.wireOp",EDGE,"E25.0.5.0"),sQuery(id+"F21.wireOp",EDGE,"E25.1.0.0"),sQuery(id+"F21.wireOp",EDGE,"E25.1.1.0"),sQuery(id+"F21.wireOp",EDGE,"E25.1.2.0"),sQuery(id+"F21.wireOp",EDGE,"E25.1.3.0"),sQuery(id+"F21.wireOp",EDGE,"E25.1.4.0"),sQuery(id+"F21.wireOp",EDGE,"E25.1.5.0"),sQuery(id+"F21.wireOp",EDGE,"E25.2.0.0"),sQuery(id+"F21.wireOp",EDGE,"E25.2.1.0"),sQuery(id+"F21.wireOp",EDGE,"E25.2.2.0"),sQuery(id+"F21.wireOp",EDGE,"E25.2.3.0"),sQuery(id+"F21.wireOp",EDGE,"E25.2.4.0"),sQuery(id+"F21.wireOp",EDGE,"E25.2.5.0"),sQuery(id+"F21.wireOp",EDGE,"E25.3.0.0"),sQuery(id+"F21.wireOp",EDGE,"E25.3.1.0"),sQuery(id+"F21.wireOp",EDGE,"E25.3.2.0"),sQuery(id+"F21.wireOp",EDGE,"E25.3.3.0"),sQuery(id+"F21.wireOp",EDGE,"E25.3.4.0"),sQuery(id+"F21.wireOp",EDGE,"E25.3.5.0"),sQuery(id+"F21.wireOp",EDGE,"E25.4.0.0"),sQuery(id+"F21.wireOp",EDGE,"E25.4.1.0"),sQuery(id+"F21.wireOp",EDGE,"E25.4.2.0"),sQuery(id+"F21.wireOp",EDGE,"E25.4.3.0"),sQuery(id+"F21.wireOp",EDGE,"E25.4.4.0"),sQuery(id+"F21.wireOp",EDGE,"E25.4.5.0"),sQuery(id+"F21.wireOp",EDGE,"E25.5.0.0"),sQuery(id+"F21.wireOp",EDGE,"E25.5.1.0"),sQuery(id+"F21.wireOp",EDGE,"E25.5.2.0"),sQuery(id+"F21.wireOp",EDGE,"E25.5.3.0"),sQuery(id+"F21.wireOp",EDGE,"E25.5.4.0"),sQuery(id+"F21.wireOp",EDGE,"E25.5.5.0"),sQuery(id+"F21.wireOp",EDGE,"E25.6.0.0"),sQuery(id+"F21.wireOp",EDGE,"E25.6.1.0"),sQuery(id+"F21.wireOp",EDGE,"E25.6.2.0"),sQuery(id+"F21.wireOp",EDGE,"E25.6.3.0"),sQuery(id+"F21.wireOp",EDGE,"E25.6.4.0"),sQuery(id+"F21.wireOp",EDGE,"E25.6.5.0"),sQuery(id+"F21.wireOp",EDGE,"E25.7.0.0"),sQuery(id+"F21.wireOp",EDGE,"E25.7.1.0"),sQuery(id+"F21.wireOp",EDGE,"E25.7.2.0"),sQuery(id+"F21.wireOp",EDGE,"E25.7.3.0"),sQuery(id+"F21.wireOp",EDGE,"E25.7.4.0"),sQuery(id+"F21.wireOp",EDGE,"E25.7.5.0"),sQuery(id+"F21.wireOp",EDGE,"E25.8.0.0"),sQuery(id+"F21.wireOp",EDGE,"E25.8.1.0"),sQuery(id+"F21.wireOp",EDGE,"E25.8.2.0"),sQuery(id+"F21.wireOp",EDGE,"E25.8.3.0"),sQuery(id+"F21.wireOp",EDGE,"E25.8.4.0"),sQuery(id+"F21.wireOp",EDGE,"E25.8.5.0"),sQuery(id+"F21.wireOp",EDGE,"E25.9.0.0"),sQuery(id+"F21.wireOp",EDGE,"E25.9.1.0"),sQuery(id+"F21.wireOp",EDGE,"E25.9.2.0"),sQuery(id+"F21.wireOp",EDGE,"E25.9.3.0"),sQuery(id+"F21.wireOp",EDGE,"E25.9.4.0"),sQuery(id+"F21.wireOp",EDGE,"E25.9.5.0"),sQuery(id+"F21.wireOp",EDGE,"E25.10.0.0"),sQuery(id+"F21.wireOp",EDGE,"E25.10.1.0"),sQuery(id+"F21.wireOp",EDGE,"E25.10.2.0"),sQuery(id+"F21.wireOp",EDGE,"E25.10.3.0"),sQuery(id+"F21.wireOp",EDGE,"E25.10.4.0"),sQuery(id+"F21.wireOp",EDGE,"E25.10.5.0"),sQuery(id+"F21.wireOp",EDGE,"E25.11.0.0"),sQuery(id+"F21.wireOp",EDGE,"E25.11.1.0"),sQuery(id+"F21.wireOp",EDGE,"E25.11.2.0"),sQuery(id+"F21.wireOp",EDGE,"E25.11.3.0"),sQuery(id+"F21.wireOp",EDGE,"E25.11.4.0"),sQuery(id+"F21.wireOp",EDGE,"E25.11.5.0"),sQuery(id+"F21.wireOp",EDGE,"E25.12.0.0"),sQuery(id+"F21.wireOp",EDGE,"E25.12.1.0"),sQuery(id+"F21.wireOp",EDGE,"E25.12.2.0"),sQuery(id+"F21.wireOp",EDGE,"E25.12.3.0"),sQuery(id+"F21.wireOp",EDGE,"E25.12.4.0"),sQuery(id+"F21.wireOp",EDGE,"E25.12.5.0")])]});
            var Q2;
            Q2=qCreatedBy(id+"F17.planeOp",FACE);
            mirror(context, id + "F23", {"entities" : qUnion([Q0, Q1]), "mirrorPlane" : qUnion([Q2])});
        }
        {
            var Q0;
            Q0=makeQuery(id+"F10.opExtrude","CAP_FACE",FACE,{"disambiguationData":[OSD([sQuery(id+"F9.wireOp",EDGE,"E7.0")])],"isStart":true});
            var sketch = newSketch(context, id + "F24", { "sketchPlane" : qUnion([Q0])});
            skCircle(sketch, "E26.0", {"center": v(393.7, 527.05) * mm, "radius": 9.53 * mm});
            skCircle(sketch, "E27.cCircle", {"center": v(393.7, 527.05) * mm, "radius": 19.05 * mm, "construction": true});
            skLineSegment(sketch, "E27.0", {"start": v(412.75, 538.05) * mm, "end": v(412.75, 516.05) * mm});
            skLineSegment(sketch, "E27.1", {"start": v(412.75, 516.05) * mm, "end": v(393.7, 505.05) * mm});
            skLineSegment(sketch, "E27.2", {"start": v(393.7, 505.05) * mm, "end": v(374.65, 516.05) * mm});
            skLineSegment(sketch, "E27.3", {"start": v(374.65, 516.05) * mm, "end": v(374.65, 538.05) * mm});
            skLineSegment(sketch, "E27.4", {"start": v(374.65, 538.05) * mm, "end": v(393.7, 549.05) * mm});
            skLineSegment(sketch, "E27.5", {"start": v(393.7, 549.05) * mm, "end": v(412.75, 538.05) * mm});
            skPoint(sketch, "E27.0.midPoint", {"position": v(412.75, 527.05) * mm});
            skCircle(sketch, "E28.0", {"center": v(-393.7, 527.05) * mm, "radius": 9.53 * mm});
            skCircle(sketch, "E29.0", {"center": v(-393.7, -527.05) * mm, "radius": 9.53 * mm});
            skCircle(sketch, "E30.0", {"center": v(393.7, -527.05) * mm, "radius": 9.53 * mm});
            skCircle(sketch, "E31.cCircle", {"center": v(-393.7, 527.05) * mm, "radius": 19.05 * mm, "construction": true});
            skLineSegment(sketch, "E31.0", {"start": v(-374.65, 538.05) * mm, "end": v(-374.65, 516.05) * mm});
            skLineSegment(sketch, "E31.1", {"start": v(-374.65, 516.05) * mm, "end": v(-393.7, 505.05) * mm});
            skLineSegment(sketch, "E31.2", {"start": v(-393.7, 505.05) * mm, "end": v(-412.75, 516.05) * mm});
            skLineSegment(sketch, "E31.3", {"start": v(-412.75, 516.05) * mm, "end": v(-412.75, 538.05) * mm});
            skLineSegment(sketch, "E31.4", {"start": v(-412.75, 538.05) * mm, "end": v(-393.7, 549.05) * mm});
            skLineSegment(sketch, "E31.5", {"start": v(-393.7, 549.05) * mm, "end": v(-374.65, 538.05) * mm});
            skPoint(sketch, "E31.0.midPoint", {"position": v(-374.65, 527.05) * mm});
            skCircle(sketch, "E32.cCircle", {"center": v(-393.7, -527.05) * mm, "radius": 19.05 * mm, "construction": true});
            skLineSegment(sketch, "E32.0", {"start": v(-374.65, -516.05) * mm, "end": v(-374.65, -538.05) * mm});
            skLineSegment(sketch, "E32.1", {"start": v(-374.65, -538.05) * mm, "end": v(-393.7, -549.05) * mm});
            skLineSegment(sketch, "E32.2", {"start": v(-393.7, -549.05) * mm, "end": v(-412.75, -538.05) * mm});
            skLineSegment(sketch, "E32.3", {"start": v(-412.75, -538.05) * mm, "end": v(-412.75, -516.05) * mm});
            skLineSegment(sketch, "E32.4", {"start": v(-412.75, -516.05) * mm, "end": v(-393.7, -505.05) * mm});
            skLineSegment(sketch, "E32.5", {"start": v(-393.7, -505.05) * mm, "end": v(-374.65, -516.05) * mm});
            skPoint(sketch, "E32.0.midPoint", {"position": v(-374.65, -527.05) * mm});
            skCircle(sketch, "E33.cCircle", {"center": v(393.7, -527.05) * mm, "radius": 19.05 * mm, "construction": true});
            skLineSegment(sketch, "E33.0", {"start": v(412.75, -516.05) * mm, "end": v(412.75, -538.05) * mm});
            skLineSegment(sketch, "E33.1", {"start": v(412.75, -538.05) * mm, "end": v(393.7, -549.05) * mm});
            skLineSegment(sketch, "E33.2", {"start": v(393.7, -549.05) * mm, "end": v(374.65, -538.05) * mm});
            skLineSegment(sketch, "E33.3", {"start": v(374.65, -538.05) * mm, "end": v(374.65, -516.05) * mm});
            skLineSegment(sketch, "E33.4", {"start": v(374.65, -516.05) * mm, "end": v(393.7, -505.05) * mm});
            skLineSegment(sketch, "E33.5", {"start": v(393.7, -505.05) * mm, "end": v(412.75, -516.05) * mm});
            skPoint(sketch, "E33.0.midPoint", {"position": v(412.75, -527.05) * mm});
            skSolve(sketch);
        }
        {
            var Q0;
            Q0 = qSketchRegion(id + "F24", true);
            extrude(context, id + "F25", {"entities" : qUnion([Q0]), "endBound" : BoundingType.UP_TO_NEXT, "oppositeDirection" : true, "depth" : 25.4 * mm, "offsetDistance" : 25.4 * mm});
        }
        {
            var Q0;
            {var subQ0=sQuery(id+"F2.wireOp",EDGE,"E1.top");Q0=makeQuery(id+"F3.boolean.opBoolean","SPLIT",FACE,{"disambiguationData":[TD([makeQuery(id+"F3.opExtrude","SWEPT_FACE",FACE,{"disambiguationData":[OSD([subQ0])]})])],"derivedFrom":makeQuery(id+"F1.opExtrude","SWEPT_FACE",FACE,{"disambiguationData":[OSD([sQuery(id+"F0.wireOp",EDGE,"E0.top")])]})});}
            cPlane(context, id + "F26", {"entities" : qUnion([Q0]), "cplaneType" : CPlaneType.OFFSET, "offset" : 101.6 * mm, "width" : 152.4 * mm, "height" : 152.4 * mm});
        }
        {
            var Q0;
            Q0=qCreatedBy(id+"F26.planeOp",FACE);
            var sketch = newSketch(context, id + "F27", { "sketchPlane" : qUnion([Q0])});
            skLineSegment(sketch, "E34.bottom", {"start": v(-317.5, 755.65) * mm, "end": v(317.5, 755.65) * mm});
            skLineSegment(sketch, "E34.top", {"start": v(-317.5, -755.65) * mm, "end": v(317.5, -755.65) * mm});
            skLineSegment(sketch, "E34.left", {"start": v(-317.5, 755.65) * mm, "end": v(-317.5, -755.65) * mm});
            skLineSegment(sketch, "E34.right", {"start": v(317.5, 755.65) * mm, "end": v(317.5, -755.65) * mm});
            skSolve(sketch);
        }
        {
            var Q0;
            Q0 = qSketchRegion(id + "F27", true);
            extrude(context, id + "F28", {"entities" : qUnion([Q0]), "depth" : 50.8 * mm, "offsetDistance" : 25.4 * mm});
        }
        {
            var Q0;
            Q0=makeQuery(id+"F28.opExtrude","CAP_FACE",FACE,{"disambiguationData":[OSD([sQuery(id+"F27.wireOp",EDGE,"E34.bottom"),sQuery(id+"F27.wireOp",EDGE,"E34.top"),sQuery(id+"F27.wireOp",EDGE,"E34.left"),sQuery(id+"F27.wireOp",EDGE,"E34.right")])],"isStart":true});
            shell(context, id + "F29", {"entities" : qUnion([Q0]), "thickness" : 2.54 * mm});
        }
        {
            var Q0;
            Q0=makeQuery(id+"F29.opShell","OFFSET_FACE",FACE,{"disambiguationData":[OSD([sQuery(id+"F27.wireOp",EDGE,"E34.right")])]});
            var sketch = newSketch(context, id + "F30", { "sketchPlane" : qUnion([Q0])});
            skCircle(sketch, "E35", {"center": v(0, -393.7) * mm, "radius": 9.53 * mm});
            skSolve(sketch);
        }
        {
            var Q0;
            Q0 = qSketchRegion(id + "F30", true);
            var Q1;
            Q1=sQuery(id+"F30.wireOp",EDGE,"E35");
            extrude(context, id + "F31", {"entities" : qUnion([Q0]), "operationType" : NewBodyOperationType.REMOVE, "surfaceEntities" : qUnion([Q1]), "endBound" : BoundingType.UP_TO_NEXT, "oppositeDirection" : true, "depth" : 25.4 * mm, "offsetDistance" : 25.4 * mm});
        }
        {
            var Q0;
            Q0=qCreatedBy(id+"F26.planeOp",FACE);
            cPlane(context, id + "F32", {"entities" : qUnion([Q0]), "cplaneType" : CPlaneType.OFFSET, "offset" : 25.4 * mm, "width" : 152.4 * mm, "height" : 152.4 * mm});
        }
        {
            var Q0;
            Q0=qCreatedBy(id+"F32.planeOp",FACE);
            var sketch = newSketch(context, id + "F33", { "sketchPlane" : qUnion([Q0])});
            skLineSegment(sketch, "E36", {"start": v(314.96, 0) * mm, "end": v(441.96, 0) * mm});
            skLineSegment(sketch, "E37", {"start": v(568.96, 127) * mm, "end": v(568.96, 1130.96) * mm});
            skPoint(sketch, "E38.visualSharp", {"position": v(568.96, 0) * mm});
            skArc(sketch, "E38.filletArc", {"start": v(441.96, 0) * mm, "mid": v(531.76, 37.2) * mm, "end": v(568.96, 127) * mm});
            skSolve(sketch);
        }
        {
            var Q0;
            Q0 = qSketchRegion(id + "F30", true);
            var Q1;
            Q1 = qConstructionFilter(qBodyType(qCreatedBy(id + "F33" ,EDGE), BodyType.WIRE), ConstructionObject.NO);
            sweep(context, id + "F34", {"profiles" : qUnion([Q0]), "path" : qUnion([Q1])});
        }
        {
            var Q0;
            {var subQ0=sQuery(id+"F2.wireOp",EDGE,"E1.bottom");var subQ3=sQuery(id+"F0.wireOp",EDGE,"E0.top");Q0=makeQuery(id+"F3.boolean.opBoolean","SPLIT",FACE,{"disambiguationData":[TD([makeQuery(id+"F3.opExtrude","SWEPT_FACE",FACE,{"disambiguationData":[OSD([subQ0])]})])],"derivedFrom":makeQuery(id+"F1.opExtrude","SWEPT_FACE",FACE,{"disambiguationData":[OSD([subQ3])]})});}
            var sketch = newSketch(context, id + "F35", { "sketchPlane" : qUnion([Q0])});
            skCircle(sketch, "E39", {"center": v(241.3, 628.65) * mm, "radius": 9.53 * mm});
            skSolve(sketch);
        }
        {
            var Q0;
            Q0=makeQuery(id+"F1.opExtrude","SWEPT_FACE",FACE,{"disambiguationData":[OSD([sQuery(id+"F0.wireOp",EDGE,"E0.right")])]});
            cPlane(context, id + "F36", {"entities" : qUnion([Q0]), "cplaneType" : CPlaneType.OFFSET, "offset" : 25.4 * mm, "oppositeDirection" : true, "width" : 152.4 * mm, "height" : 152.4 * mm});
        }
        {
            var Q0;
            Q0=qCreatedBy(id+"F36.planeOp",FACE);
            var sketch = newSketch(context, id + "F37", { "sketchPlane" : qUnion([Q0])});
            skLineSegment(sketch, "E40", {"start": v(-628.65, -266.7) * mm, "end": v(-628.65, -292.1) * mm});
            skLineSegment(sketch, "E41", {"start": v(-654.05, -317.5) * mm, "end": v(-844.55, -317.5) * mm});
            skLineSegment(sketch, "E42", {"start": v(-882.65, -355.6) * mm, "end": v(-882.65, -406.4) * mm});
            skLineSegment(sketch, "E43", {"start": v(-920.75, -444.5) * mm, "end": v(-1107.93, -444.5) * mm});
            skPoint(sketch, "E44.visualSharp", {"position": v(-628.65, -317.5) * mm});
            skArc(sketch, "E44.filletArc", {"start": v(-654.05, -317.5) * mm, "mid": v(-636.09, -310.06) * mm, "end": v(-628.65, -292.1) * mm});
            skPoint(sketch, "E45.visualSharp", {"position": v(-882.65, -317.5) * mm});
            skLineSegment(sketch, "E46", {"start": v(-844.55, -317.5) * mm, "end": v(-844.55, -317.5) * mm});
            skArc(sketch, "E47.filletArc", {"start": v(-844.55, -317.5) * mm, "mid": v(-871.5, -328.66) * mm, "end": v(-882.65, -355.6) * mm});
            skPoint(sketch, "E48.visualSharp", {"position": v(-882.65, -444.5) * mm});
            skArc(sketch, "E48.filletArc", {"start": v(-920.75, -444.5) * mm, "mid": v(-893.8, -433.34) * mm, "end": v(-882.65, -406.4) * mm});
            skSolve(sketch);
        }
        {
            var Q0;
            Q0 = qSketchRegion(id + "F35", true);
            var Q1;
            Q1 = qConstructionFilter(qBodyType(qCreatedBy(id + "F37" ,EDGE), BodyType.WIRE), ConstructionObject.NO);
            sweep(context, id + "F38", {"profiles" : qUnion([Q0]), "path" : qUnion([Q1])});
        }
        {
            var Q0;
            Q0=makeQuery(id+"F34.opSweep","CAP_FACE",FACE,{"disambiguationData":[OSD([sQuery(id+"F30.wireOp",EDGE,"E35"),sQuery(id+"F33.wireOp",VERTEX,"E37.end")])],"isStart":false});
            shell(context, id + "F39", {"entities" : qUnion([Q0]), "thickness" : 1.27 * mm});
        }
        {
            var Q0;
            Q0=qCreatedBy(id+"F36.planeOp",FACE);
            var sketch = newSketch(context, id + "F40", { "sketchPlane" : qUnion([Q0])});
            skLineSegment(sketch, "E49.0", {"start": v(-844.55, -327.03) * mm, "end": v(-844.55, -307.98) * mm, "construction": true});
            skLineSegment(sketch, "E50", {"start": v(-844.55, -317.5) * mm, "end": v(-844.55, -317.5) * mm});
            skLineSegment(sketch, "E51", {"start": v(-882.65, -279.4) * mm, "end": v(-882.65, -225.1) * mm});
            skArc(sketch, "E52.filletArc", {"start": v(-882.65, -279.4) * mm, "mid": v(-871.5, -306.34) * mm, "end": v(-844.55, -317.5) * mm});
            skSolve(sketch);
        }
        {
            var Q0;
            Q0=makeQuery(id+"F1.opExtrude","CAP_FACE",FACE,{"disambiguationData":[OSD([sQuery(id+"F0.wireOp",EDGE,"E0.bottom"),sQuery(id+"F0.wireOp",EDGE,"E0.top"),sQuery(id+"F0.wireOp",EDGE,"E0.left"),sQuery(id+"F0.wireOp",EDGE,"E0.right")])],"isStart":false});
            cPlane(context, id + "F41", {"entities" : qUnion([Q0]), "cplaneType" : CPlaneType.OFFSET, "offset" : 165.1 * mm, "width" : 152.4 * mm, "height" : 152.4 * mm});
        }
        {
            var Q0;
            Q0=qCreatedBy(id+"F41.planeOp",FACE);
            var sketch = newSketch(context, id + "F42", { "sketchPlane" : qUnion([Q0])});
            skCircle(sketch, "E53.0", {"center": v(241.3, -317.5) * mm, "radius": 9.52 * mm});
            skSolve(sketch);
        }
        {
            var Q0;
            Q0 = qSketchRegion(id + "F42", true);
            var Q1;
            Q1 = qConstructionFilter(qBodyType(qCreatedBy(id + "F40" ,EDGE), BodyType.WIRE), ConstructionObject.NO);
            sweep(context, id + "F43", {"operationType" : NewBodyOperationType.ADD, "profiles" : qUnion([Q0]), "path" : qUnion([Q1])});
        }
        {
            var Q0;
            Q0=makeQuery(id+"F43.opSweep","CAP_FACE",FACE,{"disambiguationData":[OSD([sQuery(id+"F40.wireOp",VERTEX,"E51.end"),sQuery(id+"F42.wireOp",EDGE,"E53.0")])],"isStart":false});
            var Q1;
            Q1=makeQuery(id+"F38.opSweep","CAP_FACE",FACE,{"disambiguationData":[OSD([sQuery(id+"F35.wireOp",EDGE,"E39"),sQuery(id+"F37.wireOp",VERTEX,"E43.end")])],"isStart":false});
            shell(context, id + "F44", {"entities" : qUnion([Q0, Q1]), "thickness" : 1.27 * mm});
        }
    });
